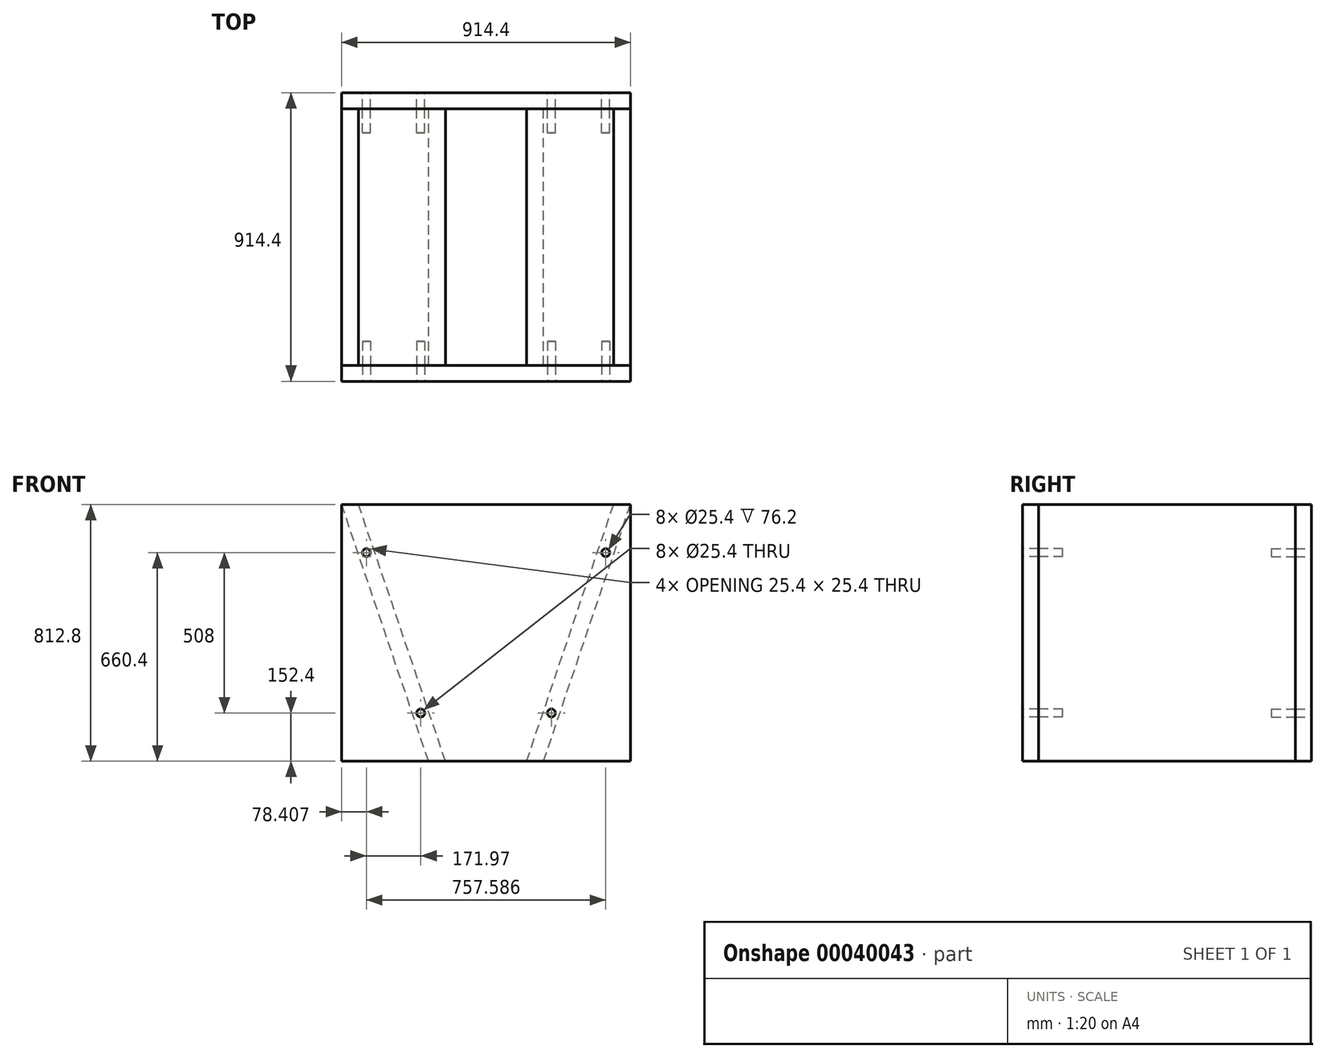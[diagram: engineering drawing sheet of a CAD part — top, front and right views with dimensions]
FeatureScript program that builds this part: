
annotation { "Feature Type Name" : "Feature", "Feature Type Description" : "" }
export const myFeature = defineFeature(function(context is Context, id is Id, definition is map)
    precondition{}
    {
        {
            var Q0;
            Q0=qCreatedBy(makeId("Front.planeOp"),FACE);
            var sketch = newSketch(context, id + "F0", { "sketchPlane" : qUnion([Q0])});
            skLineSegment(sketch, "E0.top", {"start": v(-457.2, -406.4) * mm, "end": v(0, -406.4) * mm});
            skLineSegment(sketch, "E1", {"start": v(-457.2, 406.4) * mm, "end": v(-457.2, -406.4) * mm});
            skLineSegment(sketch, "E2", {"start": v(0, 406.4) * mm, "end": v(0, -406.4) * mm, "construction": true});
            skLineSegment(sketch, "E3", {"start": v(0, -290.13) * mm, "end": v(0, -406.4) * mm, "construction": true});
            skLineSegment(sketch, "E4.MirrorCS", {"start": v(457.2, 406.4) * mm, "end": v(457.2, -406.4) * mm});
            skLineSegment(sketch, "E5.MirrorCS", {"start": v(457.2, -406.4) * mm, "end": v(0, -406.4) * mm});
            skLineSegment(sketch, "E6", {"start": v(457.2, 406.4) * mm, "end": v(0, 406.4) * mm});
            skLineSegment(sketch, "E7.MirrorCS", {"start": v(-457.2, 406.4) * mm, "end": v(0, 406.4) * mm});
            skSolve(sketch);
        }
        {
            var Q0;
            Q0 = qSketchRegion(id + "F0", true);
            extrude(context, id + "F1", {"entities" : qUnion([Q0]), "depth" : 50.8 * mm});
        }
        {
            var Q0;
            Q0=makeQuery(id+"F1.opExtrude","CAP_FACE",FACE,{"disambiguationData":[OSD([sQuery(id+"F0.wireOp",EDGE,"E0.bottom"),sQuery(id+"F0.wireOp",EDGE,"E0.top"),sQuery(id+"F0.wireOp",EDGE,"c8ed0cfd-a6e5-4cc3-9247-c517e1676721.bottom"),sQuery(id+"F0.wireOp",EDGE,"E1"),sQuery(id+"F0.wireOp",EDGE,"f15eb2b9-17f3-43d4-9424-7a087c1a6e340.MirrorCS"),sQuery(id+"F0.wireOp",EDGE,"E4.MirrorCS"),sQuery(id+"F0.wireOp",EDGE,"afe1da4d-6443-4d31-97f1-2e883f5b84a70.MirrorCS"),sQuery(id+"F0.wireOp",EDGE,"E5.MirrorCS")])],"isStart":false});
            cPlane(context, id + "F2", {"entities" : qUnion([Q0]), "cplaneType" : CPlaneType.OFFSET, "offset" : 406.4 * mm, "width" : 152.4 * mm, "height" : 152.4 * mm});
        }
        {
            var Q0;
            Q0=makeQuery(id+"F1.opExtrude","CAP_FACE",FACE,{"disambiguationData":[OSD([sQuery(id+"F0.wireOp",EDGE,"E0.bottom"),sQuery(id+"F0.wireOp",EDGE,"E0.top"),sQuery(id+"F0.wireOp",EDGE,"c8ed0cfd-a6e5-4cc3-9247-c517e1676721.bottom"),sQuery(id+"F0.wireOp",EDGE,"E1"),sQuery(id+"F0.wireOp",EDGE,"f15eb2b9-17f3-43d4-9424-7a087c1a6e340.MirrorCS"),sQuery(id+"F0.wireOp",EDGE,"E4.MirrorCS"),sQuery(id+"F0.wireOp",EDGE,"afe1da4d-6443-4d31-97f1-2e883f5b84a70.MirrorCS"),sQuery(id+"F0.wireOp",EDGE,"E5.MirrorCS")])],"isStart":false});
            var sketch = newSketch(context, id + "F3", { "sketchPlane" : qUnion([Q0])});
            skPoint(sketch, "E8", {"position": v(0, -406.4) * mm});
            skLineSegment(sketch, "E9", {"start": v(403.57, 406.4) * mm, "end": v(128.42, -406.4) * mm});
            skLineSegment(sketch, "E10", {"start": v(457.2, 406.4) * mm, "end": v(182.05, -406.4) * mm});
            skLineSegment(sketch, "E11.MirrorCS", {"start": v(-403.57, 406.4) * mm, "end": v(-128.42, -406.4) * mm});
            skLineSegment(sketch, "E12.MirrorCS", {"start": v(-457.2, 406.4) * mm, "end": v(-182.05, -406.4) * mm});
            skLineSegment(sketch, "E13", {"start": v(0, 406.4) * mm, "end": v(0, -406.4) * mm, "construction": true});
            skLineSegment(sketch, "E14", {"start": v(457.2, 406.4) * mm, "end": v(403.57, 406.4) * mm, "construction": true});
            skSolve(sketch);
        }
        {
            var Q0;
            Q0=makeQuery(id+"F1.opExtrude","CAP_FACE",FACE,{"disambiguationData":[OSD([sQuery(id+"F0.wireOp",EDGE,"E0.bottom"),sQuery(id+"F0.wireOp",EDGE,"E0.top"),sQuery(id+"F0.wireOp",EDGE,"c8ed0cfd-a6e5-4cc3-9247-c517e1676721.bottom"),sQuery(id+"F0.wireOp",EDGE,"E1"),sQuery(id+"F0.wireOp",EDGE,"f15eb2b9-17f3-43d4-9424-7a087c1a6e340.MirrorCS"),sQuery(id+"F0.wireOp",EDGE,"E4.MirrorCS"),sQuery(id+"F0.wireOp",EDGE,"afe1da4d-6443-4d31-97f1-2e883f5b84a70.MirrorCS"),sQuery(id+"F0.wireOp",EDGE,"E5.MirrorCS")])],"isStart":true});
            var sketch = newSketch(context, id + "F4", { "sketchPlane" : qUnion([Q0])});
            skCircle(sketch, "E15", {"center": v(-378.8, 254) * mm, "radius": 12.7 * mm});
            skCircle(sketch, "E16", {"center": v(-206.82, -254) * mm, "radius": 12.7 * mm});
            skLineSegment(sketch, "E17", {"start": v(-430.38, 406.4) * mm, "end": v(-155.23, -406.4) * mm, "construction": true});
            skCircle(sketch, "E18.MirrorC", {"center": v(378.8, 254) * mm, "radius": 12.7 * mm});
            skCircle(sketch, "E19.MirrorC", {"center": v(206.82, -254) * mm, "radius": 12.7 * mm});
            skSolve(sketch);
        }
        {
            var Q0;
            Q0 = qSketchRegion(id + "F4", true);
            var Q1;
            Q1=makeQuery(id+"F1.opExtrude","CAP_FACE",FACE,{"disambiguationData":[OSD([sQuery(id+"F0.wireOp",EDGE,"E0.top"),sQuery(id+"F0.wireOp",EDGE,"E1"),sQuery(id+"F0.wireOp",EDGE,"E4.MirrorCS"),sQuery(id+"F0.wireOp",EDGE,"E5.MirrorCS"),sQuery(id+"F0.wireOp",EDGE,"E6"),sQuery(id+"F0.wireOp",EDGE,"E7.MirrorCS")])],"isStart":false});
            extrude(context, id + "F5", {"entities" : qUnion([Q0]), "operationType" : NewBodyOperationType.REMOVE, "endBound" : BoundingType.UP_TO_SURFACE, "oppositeDirection" : true, "endBoundEntityFace" : qUnion([Q1]), "depth" : 152.4 * mm});
        }
        {
            var Q0;
            Q0=makeQuery(id+"F1.opExtrude","SWEPT_BODY",BODY,{"disambiguationData":[OSD([sQuery(id+"F0.wireOp",EDGE,"E0.bottom"),sQuery(id+"F0.wireOp",EDGE,"E0.top"),sQuery(id+"F0.wireOp",EDGE,"c8ed0cfd-a6e5-4cc3-9247-c517e1676721.bottom"),sQuery(id+"F0.wireOp",EDGE,"E1"),sQuery(id+"F0.wireOp",EDGE,"f15eb2b9-17f3-43d4-9424-7a087c1a6e340.MirrorCS"),sQuery(id+"F0.wireOp",EDGE,"E4.MirrorCS"),sQuery(id+"F0.wireOp",EDGE,"afe1da4d-6443-4d31-97f1-2e883f5b84a70.MirrorCS"),sQuery(id+"F0.wireOp",EDGE,"E5.MirrorCS")])]});
            var Q1;
            Q1=qCreatedBy(id+"F2.planeOp",FACE);
            mirror(context, id + "F6", {"entities" : qUnion([Q0]), "mirrorPlane" : qUnion([Q1])});
        }
        {
            var Q0;
            {var subQ1=sQuery(id+"F3.wireOp",EDGE,"E11.MirrorCS");Q0=makeQuery(id+"F3.imprint","IMPRINT",FACE,{"disambiguationData":[TD([[makeQuery(id+"F3.imprint","IMPRINT",EDGE,{"derivedFrom":subQ1}),-1.0]])]});}
            var Q1;
            {var subQ1=sQuery(id+"F3.wireOp",EDGE,"E9");Q1=makeQuery(id+"F3.imprint","IMPRINT",FACE,{"disambiguationData":[TD([[makeQuery(id+"F3.imprint","IMPRINT",EDGE,{"derivedFrom":subQ1}),1.0]])]});}
            var Q2;
            Q2=makeQuery(id+"F6.opPattern","COPY",FACE,{"derivedFrom":makeQuery(id+"F1.opExtrude","CAP_FACE",FACE,{"disambiguationData":[OSD([sQuery(id+"F0.wireOp",EDGE,"E0.top"),sQuery(id+"F0.wireOp",EDGE,"E1"),sQuery(id+"F0.wireOp",EDGE,"E4.MirrorCS"),sQuery(id+"F0.wireOp",EDGE,"E5.MirrorCS"),sQuery(id+"F0.wireOp",EDGE,"E6"),sQuery(id+"F0.wireOp",EDGE,"E7.MirrorCS")])],"isStart":false}),"instanceName":"1"});
            extrude(context, id + "F7", {"entities" : qUnion([Q0, Q1]), "endBound" : BoundingType.UP_TO_SURFACE, "endBoundEntityFace" : qUnion([Q2]), "depth" : 25.4 * mm});
        }
        {
            var Q0;
            Q0=makeQuery(id+"F7.opExtrude","CAP_FACE",FACE,{"disambiguationData":[OSD([sQuery(id+"F0.wireOp",EDGE,"E0.top"),sQuery(id+"F0.wireOp",EDGE,"E5.MirrorCS"),sQuery(id+"F0.wireOp",EDGE,"E6"),sQuery(id+"F0.wireOp",EDGE,"E7.MirrorCS"),sQuery(id+"F3.wireOp",EDGE,"E9"),sQuery(id+"F3.wireOp",EDGE,"E10")])],"isStart":true});
            var sketch = newSketch(context, id + "F8", { "sketchPlane" : qUnion([Q0])});
            skCircle(sketch, "E20", {"center": v(-378.8, 254) * mm, "radius": 12.7 * mm});
            skCircle(sketch, "E21", {"center": v(-206.82, -254) * mm, "radius": 12.7 * mm});
            skLineSegment(sketch, "E22", {"start": v(-430.38, 406.4) * mm, "end": v(-155.23, -406.4) * mm, "construction": true});
            skLineSegment(sketch, "E23", {"start": v(0, 406.4) * mm, "end": v(0, -406.4) * mm, "construction": true});
            skCircle(sketch, "E24.MirrorC", {"center": v(378.8, 254) * mm, "radius": 12.7 * mm});
            skCircle(sketch, "E25.MirrorC", {"center": v(206.82, -254) * mm, "radius": 12.7 * mm});
            skSolve(sketch);
        }
        {
            var Q0;
            Q0=makeQuery(id+"F7.opExtrude","CAP_FACE",FACE,{"disambiguationData":[OSD([sQuery(id+"F0.wireOp",EDGE,"E0.top"),sQuery(id+"F0.wireOp",EDGE,"E5.MirrorCS"),sQuery(id+"F0.wireOp",EDGE,"E6"),sQuery(id+"F0.wireOp",EDGE,"E7.MirrorCS"),sQuery(id+"F3.wireOp",EDGE,"E11.MirrorCS"),sQuery(id+"F3.wireOp",EDGE,"E12.MirrorCS")])],"isStart":false});
            var sketch = newSketch(context, id + "F9", { "sketchPlane" : qUnion([Q0])});
            skCircle(sketch, "E26", {"center": v(-378.8, 254) * mm, "radius": 12.7 * mm});
            skCircle(sketch, "E27", {"center": v(-206.82, -254) * mm, "radius": 12.7 * mm});
            skLineSegment(sketch, "E28", {"start": v(-430.38, 406.4) * mm, "end": v(-155.23, -406.4) * mm, "construction": true});
            skLineSegment(sketch, "E29", {"start": v(0, 406.4) * mm, "end": v(0, -406.4) * mm, "construction": true});
            skCircle(sketch, "E30.MirrorC", {"center": v(378.8, 254) * mm, "radius": 12.7 * mm});
            skCircle(sketch, "E31.MirrorC", {"center": v(206.82, -254) * mm, "radius": 12.7 * mm});
            skLineSegment(sketch, "E32", {"start": v(-457.2, 406.4) * mm, "end": v(-403.57, 406.4) * mm, "construction": true});
            skSolve(sketch);
        }
        {
            var Q0;
            Q0 = qSketchRegion(id + "F8", true);
            extrude(context, id + "F10", {"entities" : qUnion([Q0]), "operationType" : NewBodyOperationType.REMOVE, "oppositeDirection" : true, "depth" : 76.2 * mm});
        }
        {
            var Q0;
            Q0 = qSketchRegion(id + "F9", true);
            extrude(context, id + "F11", {"entities" : qUnion([Q0]), "operationType" : NewBodyOperationType.REMOVE, "oppositeDirection" : true, "depth" : 76.2 * mm});
        }
    });
